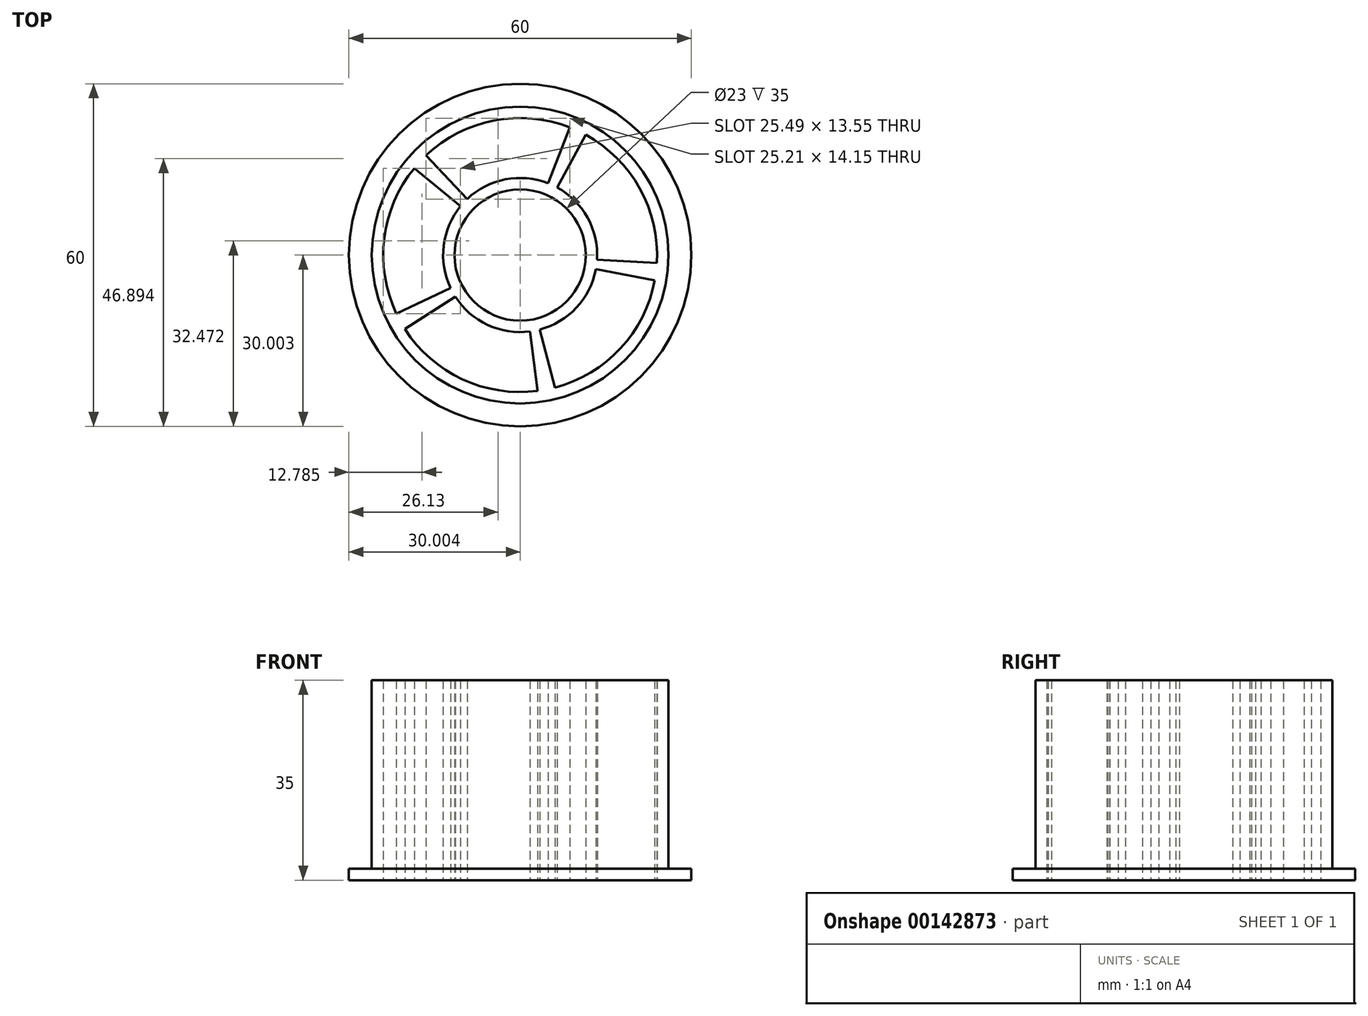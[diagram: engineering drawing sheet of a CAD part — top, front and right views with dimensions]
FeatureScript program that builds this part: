
annotation { "Feature Type Name" : "Feature", "Feature Type Description" : "" }
export const myFeature = defineFeature(function(context is Context, id is Id, definition is map)
    precondition{}
    {
        {
            var Q0;
            Q0=qCreatedBy(makeId("Top.planeOp"),FACE);
            var sketch = newSketch(context, id + "F0", { "sketchPlane" : qUnion([Q0])});
            skCircle(sketch, "E0", {"center": v(2.41, 2.95) * mm, "radius": 26 * mm});
            skCircle(sketch, "E1", {"center": v(2.41, 2.95) * mm, "radius": 11.5 * mm});
            skCircle(sketch, "E2", {"center": v(2.41, 2.95) * mm, "radius": 13.5 * mm});
            skCircle(sketch, "E3", {"center": v(2.41, 2.95) * mm, "radius": 24 * mm});
            skCircle(sketch, "E4.cCircle", {"center": v(2.41, 2.95) * mm, "radius": 24 * mm, "construction": true});
            skLineSegment(sketch, "E4.0", {"start": v(-3.66, 26.17) * mm, "end": v(11.14, 25.3) * mm, "construction": true});
            skLineSegment(sketch, "E4.1", {"start": v(11.14, 25.3) * mm, "end": v(22.62, 15.9) * mm, "construction": true});
            skLineSegment(sketch, "E4.2", {"start": v(22.62, 15.9) * mm, "end": v(26.37, 1.56) * mm, "construction": true});
            skLineSegment(sketch, "E4.3", {"start": v(26.37, 1.56) * mm, "end": v(20.98, -12.26) * mm, "construction": true});
            skLineSegment(sketch, "E4.4", {"start": v(20.98, -12.26) * mm, "end": v(8.5, -20.27) * mm, "construction": true});
            skLineSegment(sketch, "E4.5", {"start": v(8.5, -20.27) * mm, "end": v(-6.32, -19.4) * mm, "construction": true});
            skLineSegment(sketch, "E4.6", {"start": v(-6.32, -19.4) * mm, "end": v(-17.79, -10) * mm, "construction": true});
            skLineSegment(sketch, "E4.7", {"start": v(-17.79, -10) * mm, "end": v(-21.55, 4.35) * mm, "construction": true});
            skLineSegment(sketch, "E4.8", {"start": v(-21.55, 4.35) * mm, "end": v(-16.15, 18.16) * mm, "construction": true});
            skLineSegment(sketch, "E4.9", {"start": v(-16.15, 18.16) * mm, "end": v(-3.66, 26.17) * mm, "construction": true});
            skLineSegment(sketch, "E5.0", {"start": v(-0.66, 26.75) * mm, "end": v(13.92, 24.02) * mm, "construction": true});
            skLineSegment(sketch, "E5.1", {"start": v(13.92, 24.02) * mm, "end": v(24.1, 13.23) * mm, "construction": true});
            skLineSegment(sketch, "E5.2", {"start": v(24.1, 13.23) * mm, "end": v(26, -1.48) * mm, "construction": true});
            skLineSegment(sketch, "E5.3", {"start": v(26, -1.48) * mm, "end": v(18.9, -14.5) * mm, "construction": true});
            skLineSegment(sketch, "E5.4", {"start": v(18.9, -14.5) * mm, "end": v(5.5, -20.85) * mm, "construction": true});
            skLineSegment(sketch, "E5.5", {"start": v(5.5, -20.85) * mm, "end": v(-9.09, -18.11) * mm, "construction": true});
            skLineSegment(sketch, "E5.6", {"start": v(-9.09, -18.11) * mm, "end": v(-19.27, -7.33) * mm, "construction": true});
            skLineSegment(sketch, "E5.7", {"start": v(-19.27, -7.33) * mm, "end": v(-21.17, 7.38) * mm, "construction": true});
            skLineSegment(sketch, "E5.8", {"start": v(-21.17, 7.38) * mm, "end": v(-14.07, 20.4) * mm, "construction": true});
            skLineSegment(sketch, "E5.9", {"start": v(-14.07, 20.4) * mm, "end": v(-0.66, 26.75) * mm, "construction": true});
            skLineSegment(sketch, "E6", {"start": v(-3.66, 26.17) * mm, "end": v(-3.47, 25.42) * mm});
            skLineSegment(sketch, "E7", {"start": v(-0.66, 26.75) * mm, "end": v(-0.56, 26) * mm});
            skLineSegment(sketch, "E8", {"start": v(18.9, -14.5) * mm, "end": v(18.36, -13.93) * mm});
            skLineSegment(sketch, "E9", {"start": v(20.98, -12.26) * mm, "end": v(20.38, -11.77) * mm});
            skLineSegment(sketch, "E10", {"start": v(26, -1.48) * mm, "end": v(15.68, 0.46) * mm});
            skLineSegment(sketch, "E11", {"start": v(26.37, 1.56) * mm, "end": v(15.9, 2.17) * mm});
            skLineSegment(sketch, "E12", {"start": v(24.1, 13.23) * mm, "end": v(23.4, 12.9) * mm});
            skLineSegment(sketch, "E13", {"start": v(22.62, 15.9) * mm, "end": v(21.97, 15.5) * mm});
            skLineSegment(sketch, "E14", {"start": v(11.14, 25.3) * mm, "end": v(7.32, 15.53) * mm});
            skLineSegment(sketch, "E15", {"start": v(-9.09, -18.11) * mm, "end": v(-10.13, -16.28) * mm});
            skLineSegment(sketch, "E16.trimOffspring", {"start": v(-6.86, 12.77) * mm, "end": v(-14.07, 20.4) * mm});
            skLineSegment(sketch, "E17.trimOffspring", {"start": v(-8.03, 11.5) * mm, "end": v(-16.15, 18.16) * mm});
            skLineSegment(sketch, "E18.trimOffspring", {"start": v(-20.42, 7.24) * mm, "end": v(-21.17, 7.38) * mm});
            skLineSegment(sketch, "E19.trimOffspring", {"start": v(-20.78, 4.3) * mm, "end": v(-21.55, 4.35) * mm});
            skLineSegment(sketch, "E20.trimOffspring", {"start": v(-9.79, -2.82) * mm, "end": v(-19.3, -7.33) * mm});
            skLineSegment(sketch, "E21.trimOffspring", {"start": v(-8.95, -4.33) * mm, "end": v(-17.79, -10) * mm});
            skLineSegment(sketch, "E22.trimOffspring", {"start": v(-6.04, -18.68) * mm, "end": v(-6.32, -19.4) * mm});
            skLineSegment(sketch, "E23.trimOffspring", {"start": v(4.14, -10.44) * mm, "end": v(5.5, -20.85) * mm});
            skLineSegment(sketch, "E24.trimOffspring", {"start": v(5.83, -10.1) * mm, "end": v(8.5, -20.27) * mm});
            skLineSegment(sketch, "E25.trimOffspring", {"start": v(8.88, 14.8) * mm, "end": v(13.92, 24.02) * mm});
            skCircle(sketch, "E26", {"center": v(2.41, 2.95) * mm, "radius": 30 * mm});
            skSolve(sketch);
        }
        {
            var Q0;
            {var subQ0=sQuery(id+"F0.wireOp",EDGE,"E18.trimOffspring");Q0=makeQuery(id+"F0.imprint","IMPRINT",FACE,{"disambiguationData":[TD([[makeQuery(id+"F0.imprint","IMPRINT",EDGE,{"derivedFrom":subQ0}),1.0]])]});}
            var Q1;
            {var subQ3=sQuery(id+"F0.wireOp",EDGE,"E21.trimOffspring");Q1=makeQuery(id+"F0.imprint","IMPRINT",FACE,{"disambiguationData":[TD([[makeQuery(id+"F0.imprint","IMPRINT",EDGE,{"derivedFrom":subQ3}),-1.0]])]});}
            var Q2;
            {var subQ0=sQuery(id+"F0.wireOp",EDGE,"E15");Q2=makeQuery(id+"F0.imprint","IMPRINT",FACE,{"disambiguationData":[TD([[makeQuery(id+"F0.imprint","IMPRINT",EDGE,{"derivedFrom":subQ0}),-1.0]])]});}
            var Q3;
            {var subQ0=sQuery(id+"F0.wireOp",EDGE,"E23.trimOffspring");Q3=makeQuery(id+"F0.imprint","IMPRINT",FACE,{"disambiguationData":[TD([[makeQuery(id+"F0.imprint","IMPRINT",EDGE,{"derivedFrom":subQ0}),1.0]])]});}
            var Q4;
            {var subQ0=sQuery(id+"F0.wireOp",EDGE,"E8");Q4=makeQuery(id+"F0.imprint","IMPRINT",FACE,{"disambiguationData":[TD([[makeQuery(id+"F0.imprint","IMPRINT",EDGE,{"derivedFrom":subQ0}),-1.0]])]});}
            var Q5;
            {var subQ0=sQuery(id+"F0.wireOp",EDGE,"E10");Q5=makeQuery(id+"F0.imprint","IMPRINT",FACE,{"disambiguationData":[TD([[makeQuery(id+"F0.imprint","IMPRINT",EDGE,{"derivedFrom":subQ0}),-1.0]])]});}
            var Q6;
            {var subQ0=sQuery(id+"F0.wireOp",EDGE,"E12");Q6=makeQuery(id+"F0.imprint","IMPRINT",FACE,{"disambiguationData":[TD([[makeQuery(id+"F0.imprint","IMPRINT",EDGE,{"derivedFrom":subQ0}),-1.0]])]});}
            var Q7;
            {var subQ0=sQuery(id+"F0.wireOp",EDGE,"E14");Q7=makeQuery(id+"F0.imprint","IMPRINT",FACE,{"disambiguationData":[TD([[makeQuery(id+"F0.imprint","IMPRINT",EDGE,{"derivedFrom":subQ0}),1.0]])]});}
            var Q8;
            {var subQ0=sQuery(id+"F0.wireOp",EDGE,"E6");Q8=makeQuery(id+"F0.imprint","IMPRINT",FACE,{"disambiguationData":[TD([[makeQuery(id+"F0.imprint","IMPRINT",EDGE,{"derivedFrom":subQ0}),1.0]])]});}
            var Q9;
            {var subQ0=sQuery(id+"F0.wireOp",EDGE,"E16.trimOffspring");Q9=makeQuery(id+"F0.imprint","IMPRINT",FACE,{"disambiguationData":[TD([[makeQuery(id+"F0.imprint","IMPRINT",EDGE,{"derivedFrom":subQ0}),1.0]])]});}
            var Q10;
            Q10=makeQuery(id+"F0.imprint","IMPRINT",FACE,{"disambiguationData":[TD([[makeQuery(id+"F0.imprint","IMPRINT",EDGE,{"derivedFrom":sQuery(id+"F0.wireOp",EDGE,"E1")}),-1.0]])]});
            var Q11;
            Q11=makeQuery(id+"F0.imprint","IMPRINT",FACE,{"disambiguationData":[TD([[makeQuery(id+"F0.imprint","IMPRINT",EDGE,{"derivedFrom":sQuery(id+"F0.wireOp",EDGE,"E0")}),1.0]])]});
            extrude(context, id + "F1", {"entities" : qUnion([Q0, Q1, Q2, Q3, Q4, Q5, Q6, Q7, Q8, Q9, Q10, Q11]), "depth" : 35 * mm});
        }
        {
            var Q0;
            Q0=makeQuery(id+"F0.imprint","IMPRINT",FACE,{"disambiguationData":[TD([[makeQuery(id+"F0.imprint","IMPRINT",EDGE,{"derivedFrom":sQuery(id+"F0.wireOp",EDGE,"E0")}),-1.0]])]});
            extrude(context, id + "F2", {"entities" : qUnion([Q0]), "operationType" : NewBodyOperationType.ADD, "depth" : 2 * mm});
        }
    });
